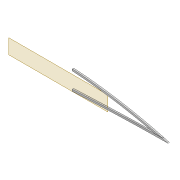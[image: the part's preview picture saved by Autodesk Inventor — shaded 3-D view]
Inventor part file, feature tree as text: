
AUTODESK INVENTOR PART (.ipt)
format: ipt  version: 2022 (Build 260153000, 153)  size: 415,232 bytes
history: native  units: mm
features: extrude x8, sketch x7, projected_geometry x6, fillet x2, shell x1, plane x1
ambient origin geometry x8: Origin, YZ Plane, XZ Plane, XY Plane, X Axis, Y Axis, Z Axis, Center Point
bodies: Solid1 (feature_tree)
feature tree (25):
  extrude  "Extrusion1"  Depth=4.0mm
  shell  "Shell1"  Thickness=2.0mm
  extrude  "Extrusion8"  Depth=5.9mm
  extrude  "Extrusion3"  Depth=10.0mm TaperAngle=0.0deg
  extrude  "Extrusion4"  Depth=4.0mm
  fillet  "Fillet1"  Radius=5.0mm
  sketch  "Sketch10"  dims[d22=4.0mm d23=0.0mm d31=2.0mm d32=5.0mm]
  extrude  "Extrusion5"  Depth=2.5mm
  plane  "Work Plane2"
  extrude  "Extrusion9"  Depth=1.6mm
  fillet  "Fillet2"  Radius=2.5mm
  extrude  "Extrusion10"  Depth=4.0mm
  extrude  "Extrusion11"  Depth=4.0mm TaperAngle=0.0deg
  sketch  "Sketch3"  dims[d0=4.0mm d1=0.0mm d2=5.0mm d7=2.0mm]
  sketch  "Sketch8"  dims[d8=2.0mm d9=5.9mm]
  sketch  "Sketch9"  dims[d13=10.0mm d14=0.0mm d16=10.0mm d17=0.0mm]
  projected_geometry  "Projected Loop4"
  projected_geometry  "Projected Loop10"
  sketch  "Sketch24"  dims[d34=1.6mm d35=2.5mm]
  projected_geometry  "Projected Loop11"
  projected_geometry  "Projected Loop12"
  projected_geometry  "Projected Loop13"
  sketch  "Sketch26"  dims[d37=5.0mm d38=1.6mm d40=2.5mm]
  projected_geometry  "Projected Loop14"
  sketch  "Sketch27"  dims[d62=80.0mm d63=6.0mm d64=4.0mm d65=0.0mm d66=3.0mm d67=12.0mm d68=5.0mm d69=19.0mm d70=12.0mm d71=3.05mm d72=10.0mm d73=0.0mm d74=2.0mm d75=100.0mm d76=20.0mm d77=0.5mm d78=10.0mm d79=0.0mm d80=10.0mm d81=0.0mm]
